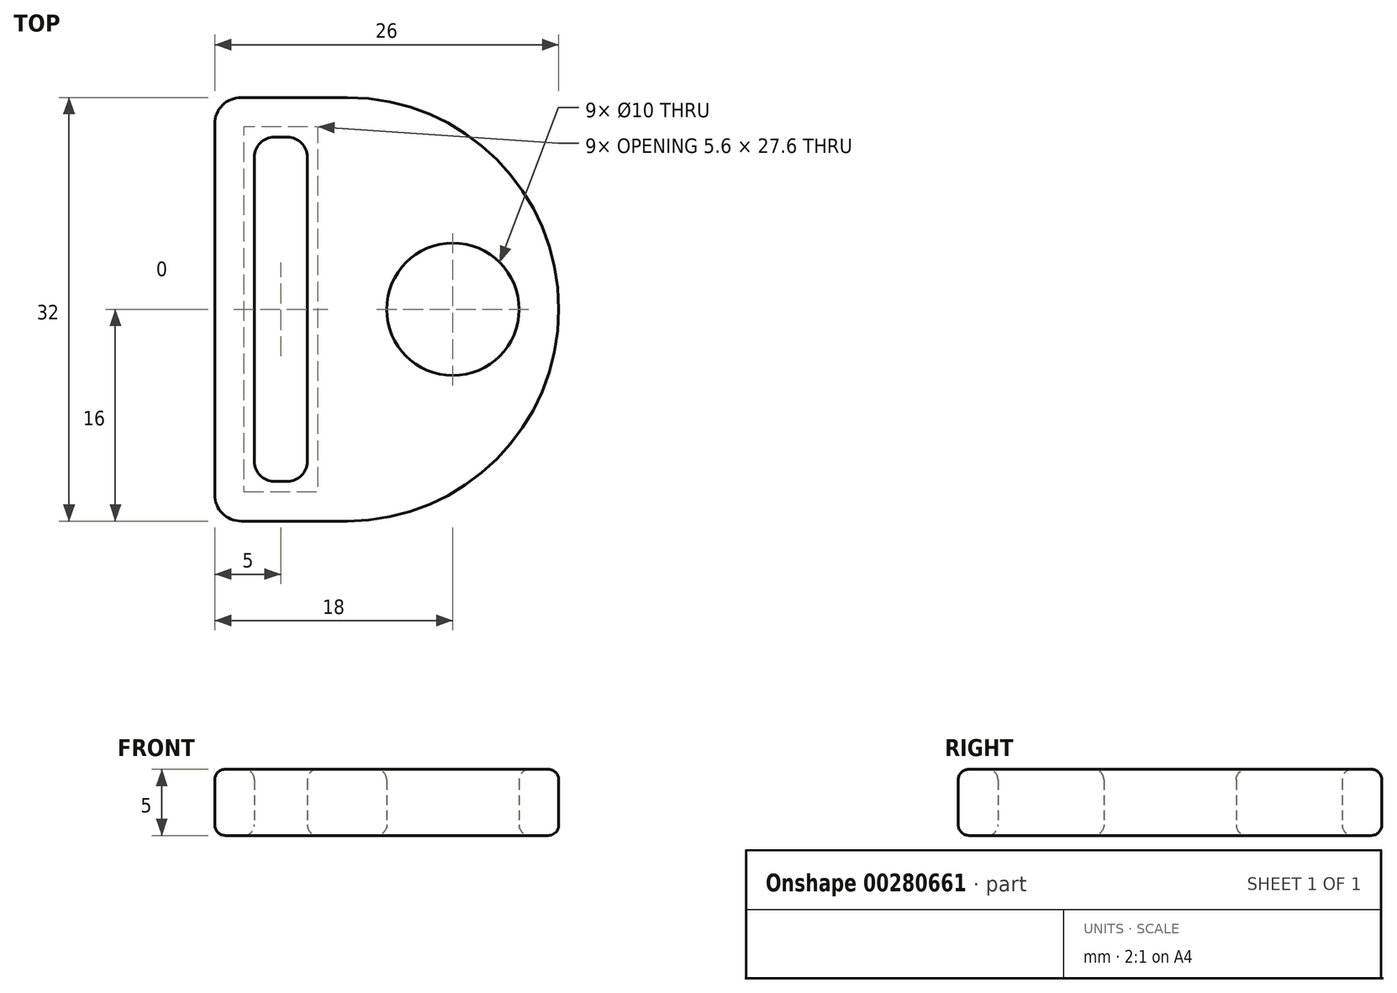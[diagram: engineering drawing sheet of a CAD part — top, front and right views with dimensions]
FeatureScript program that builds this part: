
annotation { "Feature Type Name" : "Feature", "Feature Type Description" : "" }
export const myFeature = defineFeature(function(context is Context, id is Id, definition is map)
    precondition{}
    {
        {
            var Q0;
            Q0=qCreatedBy(makeId("Top.planeOp"),FACE);
            var sketch = newSketch(context, id + "F0", { "sketchPlane" : qUnion([Q0])});
            skLineSegment(sketch, "E0", {"start": v(5, 16) * mm, "end": v(5, -16) * mm});
            skArc(sketch, "E1", {"start": v(5, 16) * mm, "mid": v(21, 0) * mm, "end": v(5, -16) * mm});
            skLineSegment(sketch, "E2.bottom", {"start": v(5, 16) * mm, "end": v(-3, 16) * mm});
            skLineSegment(sketch, "E2.top", {"start": v(5, -16) * mm, "end": v(-3, -16) * mm});
            skLineSegment(sketch, "E2.left", {"start": v(5, 16) * mm, "end": v(5, -16) * mm, "construction": true});
            skLineSegment(sketch, "E2.right", {"start": v(-5, 14) * mm, "end": v(-5, -14) * mm});
            skLineSegment(sketch, "E3.bottom", {"start": v(-0.5, -13) * mm, "end": v(0.5, -13) * mm});
            skLineSegment(sketch, "E3.top", {"start": v(-0.5, 13) * mm, "end": v(0.5, 13) * mm});
            skLineSegment(sketch, "E3.left", {"start": v(-2, -11.5) * mm, "end": v(-2, 11.5) * mm});
            skLineSegment(sketch, "E3.right", {"start": v(2, -11.5) * mm, "end": v(2, 11.5) * mm});
            skPoint(sketch, "E3.middle", {"position": v(0, 0) * mm});
            skCircle(sketch, "E4", {"center": v(13, 0) * mm, "radius": 5 * mm});
            skPoint(sketch, "E5.visualSharp", {"position": v(-5, 16) * mm});
            skArc(sketch, "E5.filletArc", {"start": v(-3, 16) * mm, "mid": v(-4.41, 15.41) * mm, "end": v(-5, 14) * mm});
            skPoint(sketch, "E6.visualSharp", {"position": v(-5, -16) * mm});
            skArc(sketch, "E6.filletArc", {"start": v(-5, -14) * mm, "mid": v(-4.41, -15.41) * mm, "end": v(-3, -16) * mm});
            skPoint(sketch, "E7.visualSharp", {"position": v(-2, 13) * mm});
            skArc(sketch, "E7.filletArc", {"start": v(-0.5, 13) * mm, "mid": v(-1.56, 12.56) * mm, "end": v(-2, 11.5) * mm});
            skPoint(sketch, "E8.visualSharp", {"position": v(2, 13) * mm});
            skArc(sketch, "E8.filletArc", {"start": v(2, 11.5) * mm, "mid": v(1.56, 12.56) * mm, "end": v(0.5, 13) * mm});
            skPoint(sketch, "E9.visualSharp", {"position": v(2, -13) * mm});
            skArc(sketch, "E9.filletArc", {"start": v(0.5, -13) * mm, "mid": v(1.56, -12.56) * mm, "end": v(2, -11.5) * mm});
            skPoint(sketch, "E10.visualSharp", {"position": v(-2, -13) * mm});
            skArc(sketch, "E10.filletArc", {"start": v(-2, -11.5) * mm, "mid": v(-1.56, -12.56) * mm, "end": v(-0.5, -13) * mm});
            skSolve(sketch);
        }
        {
            var Q0;
            Q0=makeQuery(id+"F0.imprint","IMPRINT",FACE,{"disambiguationData":[TD([[makeQuery(id+"F0.imprint","IMPRINT",EDGE,{"derivedFrom":sQuery(id+"F0.wireOp",EDGE,"E0")}),-1.0]])]});
            var Q1;
            Q1=makeQuery(id+"F0.imprint","IMPRINT",FACE,{"disambiguationData":[TD([[makeQuery(id+"F0.imprint","IMPRINT",EDGE,{"derivedFrom":sQuery(id+"F0.wireOp",EDGE,"E0")}),1.0]])]});
            extrude(context, id + "F1", {"entities" : qUnion([Q0, Q1]), "depth" : 5 * mm});
        }
        {
            var Q0;
            Q0=makeQuery(id+"F1.opExtrude","CAP_EDGE",EDGE,{"disambiguationData":[OSD([sQuery(id+"F0.wireOp",EDGE,"E2.right")])],"isStart":false});
            var Q1;
            Q1=makeQuery(id+"F1.opExtrude","CAP_EDGE",EDGE,{"disambiguationData":[OSD([sQuery(id+"F0.wireOp",EDGE,"E1")])],"isStart":true});
            fillet(context, id + "F2", {"entities" : qUnion([Q0, Q1]), "radius" : .8 * mm, "tangentPropagation" : true, "allowEdgeOverflow" : false});
        }
        {
            var Q0;
            Q0=makeQuery(id+"F1.opExtrude","CAP_EDGE",EDGE,{"disambiguationData":[OSD([sQuery(id+"F0.wireOp",EDGE,"E3.left")])],"isStart":false});
            var Q1;
            Q1=makeQuery(id+"F1.opExtrude","CAP_EDGE",EDGE,{"disambiguationData":[OSD([sQuery(id+"F0.wireOp",EDGE,"E4")])],"isStart":false});
            var Q2;
            Q2=makeQuery(id+"F1.opExtrude","CAP_EDGE",EDGE,{"disambiguationData":[OSD([sQuery(id+"F0.wireOp",EDGE,"E3.right")])],"isStart":true});
            var Q3;
            Q3=makeQuery(id+"F1.opExtrude","CAP_EDGE",EDGE,{"disambiguationData":[OSD([sQuery(id+"F0.wireOp",EDGE,"E4")])],"isStart":true});
            fillet(context, id + "F3", {"entities" : qUnion([Q0, Q1, Q2, Q3]), "radius" : .8 * mm, "tangentPropagation" : true, "allowEdgeOverflow" : false});
        }
    });
